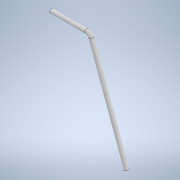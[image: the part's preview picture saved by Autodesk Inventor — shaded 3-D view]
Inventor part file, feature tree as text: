
AUTODESK INVENTOR PART (.ipt)
format: ipt  version: 2022 (Build 260153070, 153G)  size: 105,472 bytes
history: native  units: in
note: dims shown in document units (in); Inventor stores cm internally (conversion verified against a paired STEP export)
features: sketch x2, sweep x1
ambient origin geometry x8: Origin, YZ Plane, XZ Plane, XY Plane, X Axis, Y Axis, Z Axis, Center Point
bodies: Solid1 (feature_tree)
feature tree (3):
  sweep  "Sweep1"
  sketch  "Sketch3"  dims[d4=20.0in d5=0.0in]
  sketch  "Sketch4"  dims[d7=0.8in d8=20.0in d9=1.0in d10=7.0in d11=0.0in d12=0.0in d13=15.0in]
